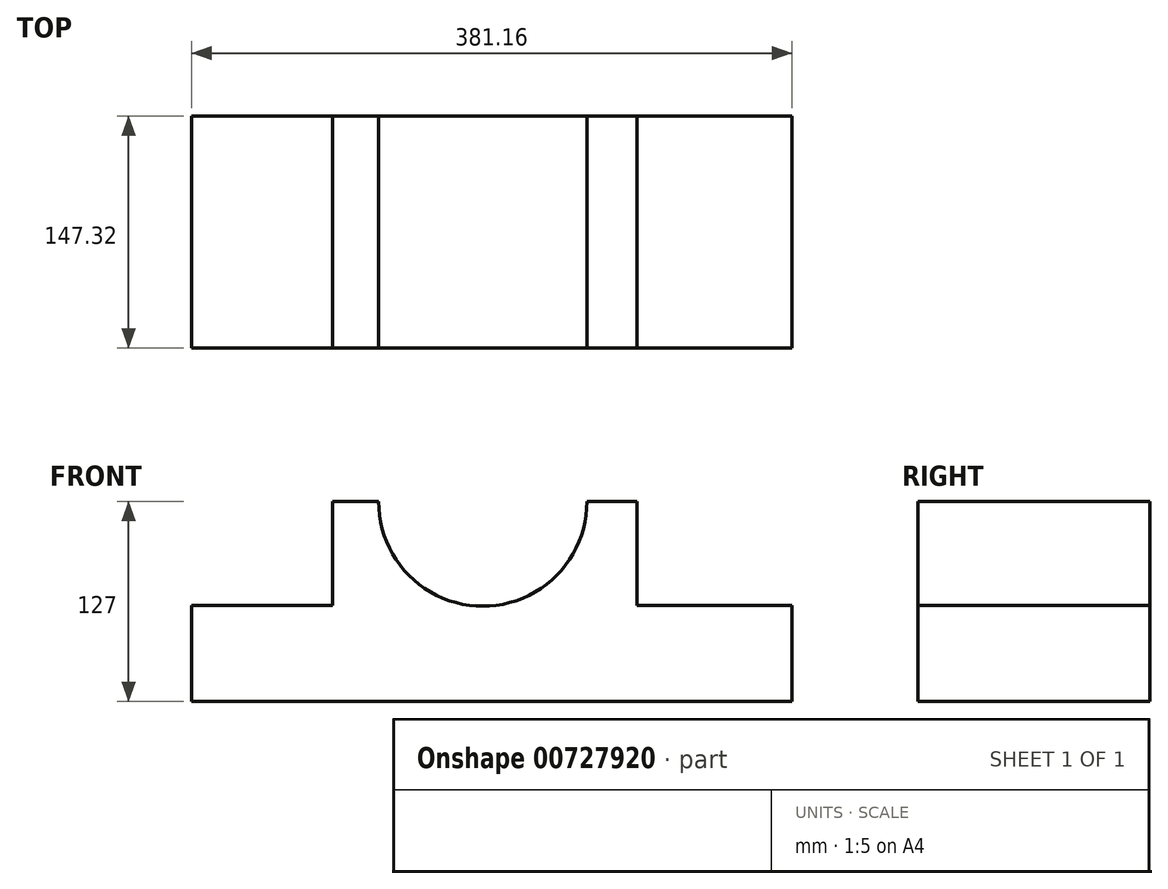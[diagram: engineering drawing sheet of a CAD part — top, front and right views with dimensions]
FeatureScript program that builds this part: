
annotation { "Feature Type Name" : "Feature", "Feature Type Description" : "" }
export const myFeature = defineFeature(function(context is Context, id is Id, definition is map)
    precondition{}
    {
        {
            var Q0;
            Q0=qCreatedBy(makeId("Front.planeOp"),FACE);
            var sketch = newSketch(context, id + "F0", { "sketchPlane" : qUnion([Q0])});
            skPoint(sketch, "E0.start.orphan", {"position": v(-188.02, -108.55) * mm});
            skLineSegment(sketch, "E1", {"start": v(-188.02, 3.62) * mm, "end": v(-188.02, -57.34) * mm});
            skLineSegment(sketch, "E2", {"start": v(-188.02, -57.34) * mm, "end": v(193.14, -57.34) * mm});
            skLineSegment(sketch, "E3", {"start": v(193.14, -57.34) * mm, "end": v(193.14, 3.62) * mm});
            skLineSegment(sketch, "E4", {"start": v(193.14, 3.62) * mm, "end": v(94.65, 3.62) * mm});
            skLineSegment(sketch, "E5", {"start": v(94.65, 3.62) * mm, "end": v(94.65, 69.66) * mm});
            skLineSegment(sketch, "E6", {"start": v(-98.4, 69.66) * mm, "end": v(-98.4, 3.62) * mm});
            skLineSegment(sketch, "E7", {"start": v(-98.4, 3.62) * mm, "end": v(-188.02, 3.62) * mm});
            skLineSegment(sketch, "E8", {"start": v(94.65, 69.66) * mm, "end": v(-98.4, 69.66) * mm});
            skSolve(sketch);
        }
        {
            var Q0;
            Q0=makeQuery(id+"F0.imprint","IMPRINT",FACE,{"disambiguationData":[TD([[makeQuery(id+"F0.imprint","IMPRINT",EDGE,{"derivedFrom":sQuery(id+"F0.wireOp",EDGE,"E1")}),1.0]])]});
            extrude(context, id + "F1", {"entities" : qUnion([Q0]), "depth" : 147.32 * mm, "offsetDistance" : 25.4 * mm});
        }
        {
            var Q0;
            Q0=makeQuery(id+"F1.opExtrude","CAP_FACE",FACE,{"disambiguationData":[OSD([sQuery(id+"F0.wireOp",EDGE,"E1"),sQuery(id+"F0.wireOp",EDGE,"E2"),sQuery(id+"F0.wireOp",EDGE,"E3"),sQuery(id+"F0.wireOp",EDGE,"E4"),sQuery(id+"F0.wireOp",EDGE,"E5"),sQuery(id+"F0.wireOp",EDGE,"E6"),sQuery(id+"F0.wireOp",EDGE,"E7"),sQuery(id+"F0.wireOp",EDGE,"E8")])],"isStart":false});
            var sketch = newSketch(context, id + "F2", { "sketchPlane" : qUnion([Q0])});
            skArc(sketch, "E9", {"start": v(-69.18, 69.66) * mm, "mid": v(-3.14, 3.16) * mm, "end": v(62.9, 69.66) * mm});
            skSolve(sketch);
        }
        {
            var Q0;
            {var subQ0=sQuery(id+"F2.wireOp",EDGE,"E9");Q0=makeQuery(id+"F2.imprint","IMPRINT",FACE,{"disambiguationData":[TD([[makeQuery(id+"F2.imprint","IMPRINT",EDGE,{"derivedFrom":subQ0}),1.0]])]});}
            extrude(context, id + "F3", {"entities" : qUnion([Q0]), "operationType" : NewBodyOperationType.REMOVE, "oppositeDirection" : true, "depth" : 147.32 * mm, "offsetDistance" : 25.4 * mm});
        }
    });
